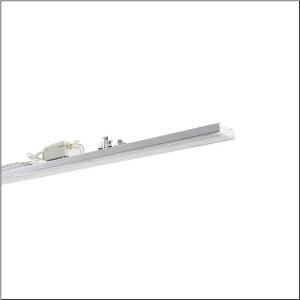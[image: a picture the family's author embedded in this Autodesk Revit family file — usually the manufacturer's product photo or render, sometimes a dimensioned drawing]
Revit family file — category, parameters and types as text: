
# Revit family: licross_r__11_recessed_extreme_mo_51tl12dv4fxge_0dac
name_source: partatom
category: Lighting Fixtures
units: mm (PartAtom-declared; Revit-internal decimal feet)

## family parameters
Cut with Voids When Loaded = No
Host = Face
Light Source = No
Part Type = Normal
Room Calculation Point = No
Round Connector Dimension = Use Diameter
Shared = No

## types (1)
- --- (1 x LED, 15360 lm, 84.1 W, 4000K)
    Apparent Load = 84 VA
    CIE Flux Codes = 67 92 99 100 100
    Color Rendering = 80
    Color Temperature = 4000K
    Default Elevation = 1800 mm
    Description = Licross® 11 Recessed extreme MO, luminaire insert, of sheet steel, coil coated, white, length: 2.250mm, width: 66mm, height: 67mm, LED rated luminous flux: 15.360lm, light colour: 840, SDCM (Standard Deviation of Colour Matching)MacAdam ≤ 2 SDCM (initial), control gear: DALI 2, with plug, 5-pole, with phase selection, mains connection: 220..240V, AC, 50/60Hz, rated input power: 84W, internal wiring halogen-free, primary optical cover: cover, of PMMA, light emission: direct distribution, primary light characteristic: symmetric, protection rating (complete): IP40, insulation class (complete): insulation class I (protective earthing), certification: CE, ENEC, VDE, UKCA, protection symbol: D if used in an environment without relevant dust loads with corresponding accessories, impact resistance: IK06, permissible ambient temperature for indoor applications: -40..+45°C, corresponds to IFS (International Featured Standards) requirements for safety and quality in the food industry, reducing of maximum allowable ambient temperature of 5°C with ceiling mounting, LABS conformity tested according to VDMA 24364:2018-05, packaging unit: 1 piece
    Height = 58 mm
    Lamp = 1 x LED
    Lamp Light Flux = 15360 lm
    Lamp Power = 84.1 W
    Lamp count = 1
    Length = 2250 mm
    Luminous efficacy = 183 lm/W
    Manufacturer = Siteco
    ModVariant = No
    Model = 51TL12DV4FXGE
    Mounting Place = Ceiling
    Mounting Type = Pendant
    Number of Poles = 1
    OnlyDefault = Yes
    Power Factor = 1
    Product Name = Licross® 11 Recessed extreme MO
    Product group = luminaire insert | ceiling pendant
    ProductGroupID = 901
    Protection Class = Protection class I
    Protection Degree = IP 40
    RLX_Detail_Level = 1
    RLX_Emergency_Light_Flux = 0 lm
    RLX_Emergency_Type = 0
    RLX_Emergency_Type_DB = No
    RlxData = <blob elided: 29505 chars, md5=39a8eb99>
    Socket = socket
    Standby Power = 0 W
    System Light Flux = 15360 lm
    System Power = 84 W
    Type Comments = factory setting: luminous flux: 100 % | dim-lin: 254 | 378 mA
    Type Image = l_1296930.jpg
    URL = http://relux.com
    VarID = @adj_090211
    Voltage = 0 V
    Weight = 0.00 kg
    Width = 66 mm

## geometry (parser evidence)
native form markers: Blend x4, Sweep x12
no freeform markers — native parametric forms only
